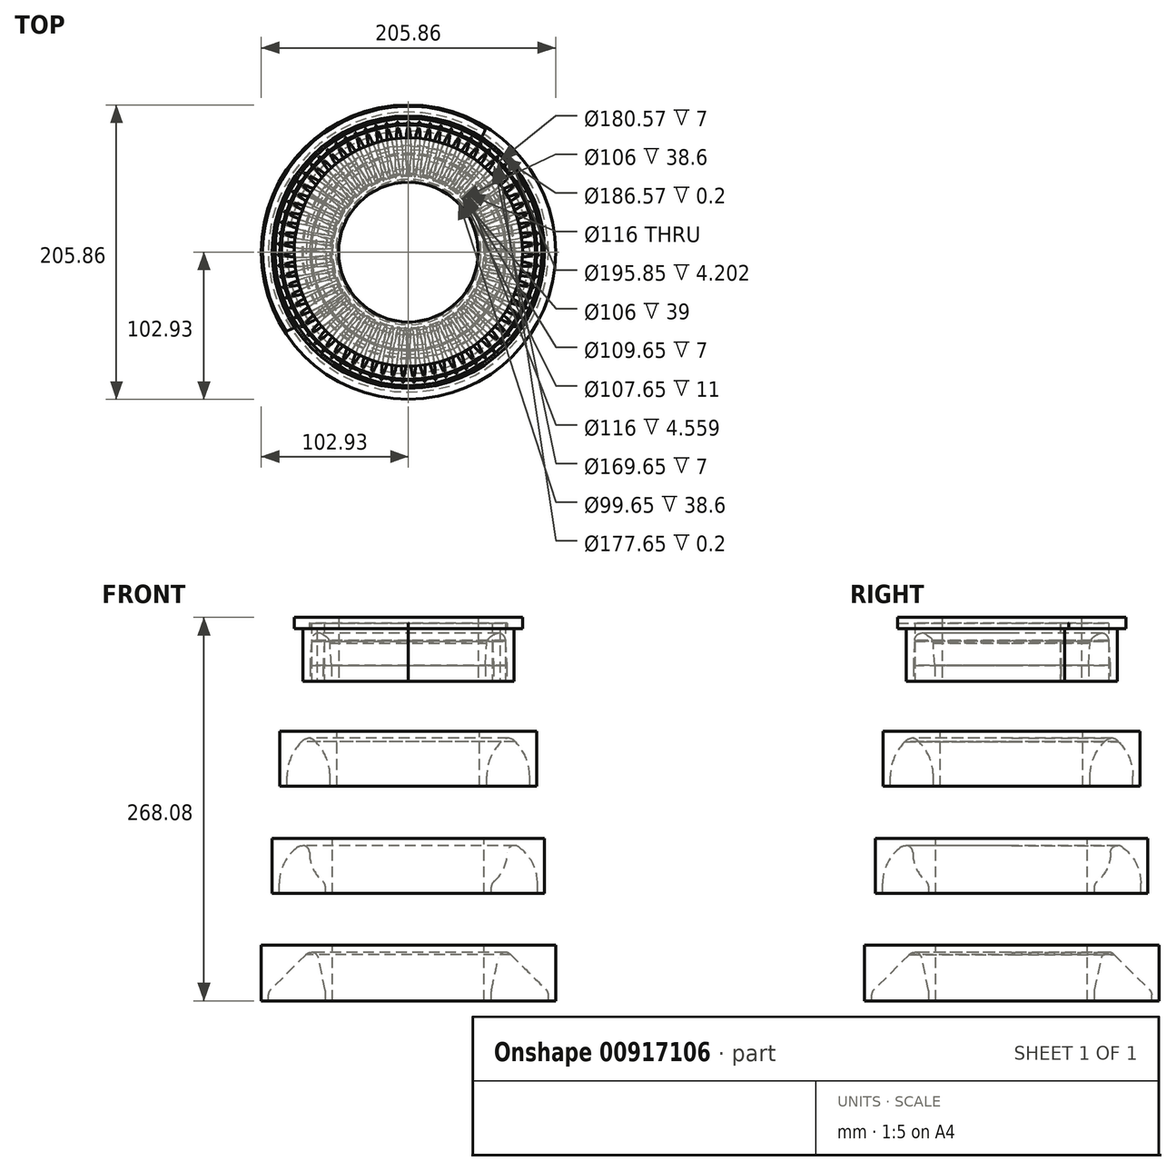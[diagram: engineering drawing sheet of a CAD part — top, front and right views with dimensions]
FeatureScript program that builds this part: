
annotation { "Feature Type Name" : "Feature", "Feature Type Description" : "" }
export const myFeature = defineFeature(function(context is Context, id is Id, definition is map)
    precondition{}
    {
        {
            var Q0;
            Q0=qCreatedBy(makeId("Front.planeOp"),FACE);
            var sketch = newSketch(context, id + "F0", { "sketchPlane" : qUnion([Q0])});
            skArc(sketch, "E0", {"start": v(57.08, 22.7) * mm, "mid": v(58.52, 23.67) * mm, "end": v(59.95, 24.66) * mm});
            skLineSegment(sketch, "E1", {"start": v(0, 0) * mm, "end": v(54.83, 0) * mm, "construction": true});
            skLineSegment(sketch, "E2", {"start": v(54.83, 0) * mm, "end": v(54.83, -7) * mm, "construction": true});
            skLineSegment(sketch, "E3", {"start": v(54.83, -7) * mm, "end": v(67.83, -7) * mm, "construction": true});
            skLineSegment(sketch, "E4", {"start": v(67.83, -7) * mm, "end": v(67.83, 0) * mm, "construction": true});
            skLineSegment(sketch, "E5", {"start": v(54.83, 0) * mm, "end": v(54.83, 3) * mm, "construction": true});
            skLineSegment(sketch, "E6", {"start": v(67.83, 0) * mm, "end": v(67.83, 3) * mm, "construction": true});
            skLineSegment(sketch, "E7", {"start": v(0, -3.7) * mm, "end": v(44, -3.7) * mm, "construction": true});
            skLineSegment(sketch, "E8", {"start": v(61.33, -7) * mm, "end": v(61.33, 37.52) * mm, "construction": true});
            skPoint(sketch, "E9.visualSharp", {"position": v(54.8, 21.25) * mm});
            skArc(sketch, "E9.filletArc", {"start": v(57.08, 22.7) * mm, "mid": v(55.43, 20.9) * mm, "end": v(54.83, 18.53) * mm});
            skPoint(sketch, "E10.visualSharp", {"position": v(67.8, 30.73) * mm});
            skArc(sketch, "E10.filletArc", {"start": v(67.83, 20.57) * mm, "mid": v(65.13, 25) * mm, "end": v(59.95, 24.66) * mm});
            skLineSegment(sketch, "E11.0", {"start": v(53.83, 0) * mm, "end": v(53.83, 3) * mm});
            skLineSegment(sketch, "E11.1", {"start": v(68.83, 0) * mm, "end": v(68.83, 3) * mm});
            skLineSegment(sketch, "E11.2", {"start": v(68.83, -8) * mm, "end": v(68.83, 0) * mm});
            skLineSegment(sketch, "E11.3", {"start": v(53.83, -8) * mm, "end": v(68.83, -8) * mm});
            skLineSegment(sketch, "E11.4", {"start": v(53.83, 0) * mm, "end": v(53.83, -8) * mm});
            skLineSegment(sketch, "E12", {"start": v(54.83, 18.53) * mm, "end": v(53.83, 3) * mm});
            skLineSegment(sketch, "E13", {"start": v(67.83, 20.57) * mm, "end": v(68.83, 3) * mm});
            skLineSegment(sketch, "E14", {"start": v(0, 0) * mm, "end": v(0, 24.2) * mm});
            skText(sketch, "E15", { "text": "Profile\n", "fontName": "OpenSans-Regular.ttf"});
            skLineSegment(sketch, "E16.0", {"start": v(48.83, 0) * mm, "end": v(48.83, -8) * mm});
            skLineSegment(sketch, "E16.1", {"start": v(48.83, 0) * mm, "end": v(48.83, 3.64) * mm});
            skLineSegment(sketch, "E16.5", {"start": v(73.83, -8) * mm, "end": v(73.83, 0) * mm});
            skLineSegment(sketch, "E17", {"start": v(48.83, 28.57) * mm, "end": v(73.83, 28.57) * mm});
            skLineSegment(sketch, "E18", {"start": v(73.83, 28.57) * mm, "end": v(73.83, 0) * mm});
            skLineSegment(sketch, "E19", {"start": v(48.83, 28.57) * mm, "end": v(48.83, 3.64) * mm});
            skLineSegment(sketch, "E20", {"start": v(53.83, -8) * mm, "end": v(48.83, -8) * mm});
            skLineSegment(sketch, "E21", {"start": v(68.83, -8) * mm, "end": v(73.83, -8) * mm});
            skLineSegment(sketch, "E22", {"start": v(0, -74.51) * mm, "end": v(54.82, -74.51) * mm, "construction": true});
            skLineSegment(sketch, "E23", {"start": v(54.83, -74.51) * mm, "end": v(54.83, -81.51) * mm});
            skLineSegment(sketch, "E24", {"start": v(54.83, -81.51) * mm, "end": v(84.83, -81.51) * mm});
            skLineSegment(sketch, "E25", {"start": v(54.83, -47.91) * mm, "end": v(121.36, -47.91) * mm, "construction": true});
            skArc(sketch, "E26", {"start": v(74.54, -50.2) * mm, "mid": v(69.83, -47.91) * mm, "end": v(65.11, -50.2) * mm});
            skLineSegment(sketch, "E27", {"start": v(69.83, -81.51) * mm, "end": v(69.83, -35.12) * mm, "construction": true});
            skLineSegment(sketch, "E28.MirrorCS", {"start": v(84.83, -74.51) * mm, "end": v(84.83, -81.51) * mm});
            skArc(sketch, "E29", {"start": v(84.83, -74.51) * mm, "mid": v(82.15, -61.31) * mm, "end": v(74.54, -50.2) * mm});
            skArc(sketch, "E30.MirrorCS", {"start": v(54.83, -74.51) * mm, "mid": v(57.5, -61.31) * mm, "end": v(65.11, -50.2) * mm});
            skLineSegment(sketch, "E31", {"start": v(0, -149.51) * mm, "end": v(58, -149.51) * mm, "construction": true});
            skLineSegment(sketch, "E32", {"start": v(58, -151.95) * mm, "end": v(58, -156.51) * mm});
            skLineSegment(sketch, "E33", {"start": v(58, -156.51) * mm, "end": v(90.28, -156.51) * mm});
            skLineSegment(sketch, "E34", {"start": v(58, -122.91) * mm, "end": v(116.03, -122.91) * mm, "construction": true});
            skArc(sketch, "E35", {"start": v(77.04, -123.84) * mm, "mid": v(71.85, -123.47) * mm, "end": v(69.14, -127.91) * mm});
            skLineSegment(sketch, "E36", {"start": v(74.14, -115.42) * mm, "end": v(74.14, -156.51) * mm, "construction": true});
            skLineSegment(sketch, "E37.MirrorCS", {"start": v(90.28, -149.51) * mm, "end": v(90.28, -156.51) * mm});
            skArc(sketch, "E38", {"start": v(90.28, -149.51) * mm, "mid": v(86.78, -135.07) * mm, "end": v(77.04, -123.84) * mm});
            skArc(sketch, "E39", {"start": v(59.77, -148.14) * mm, "mid": v(66.68, -139.06) * mm, "end": v(69.14, -127.91) * mm});
            skPoint(sketch, "E39.first.point", {"position": v(69.14, -127.91) * mm});
            skPoint(sketch, "E40.visualSharp", {"position": v(58, -149.51) * mm});
            skArc(sketch, "E40.filletArc", {"start": v(59.77, -148.14) * mm, "mid": v(58.46, -149.85) * mm, "end": v(58, -151.95) * mm});
            skLineSegment(sketch, "E41", {"start": v(0, -36.15) * mm, "end": v(0, -90.59) * mm});
            skLineSegment(sketch, "E42", {"start": v(0, -114.92) * mm, "end": v(0, -170.64) * mm});
            skLineSegment(sketch, "E43", {"start": v(84.83, -81.51) * mm, "end": v(89.83, -81.51) * mm});
            skLineSegment(sketch, "E44", {"start": v(89.83, -81.51) * mm, "end": v(89.83, -42.91) * mm});
            skLineSegment(sketch, "E45", {"start": v(89.83, -42.91) * mm, "end": v(49.83, -42.91) * mm});
            skLineSegment(sketch, "E46.MirrorCS", {"start": v(49.83, -81.51) * mm, "end": v(49.83, -42.91) * mm});
            skLineSegment(sketch, "E47", {"start": v(49.83, -81.51) * mm, "end": v(54.83, -81.51) * mm});
            skLineSegment(sketch, "E48", {"start": v(53, -117.91) * mm, "end": v(95.28, -117.91) * mm});
            skLineSegment(sketch, "E49", {"start": v(90.28, -156.51) * mm, "end": v(95.28, -156.51) * mm});
            skLineSegment(sketch, "E50", {"start": v(95.28, -156.51) * mm, "end": v(95.28, -117.91) * mm});
            skLineSegment(sketch, "E51.MirrorCS", {"start": v(53, -156.51) * mm, "end": v(53, -117.91) * mm});
            skLineSegment(sketch, "E52", {"start": v(53, -156.51) * mm, "end": v(58, -156.51) * mm});
            skText(sketch, "E53", { "text": "A", "fontName": "OpenSans-Regular.ttf"});
            skText(sketch, "E54", { "text": "B", "fontName": "OpenSans-Regular.ttf"});
            skText(sketch, "E55", { "text": "C", "fontName": "OpenSans-Regular.ttf"});
            skLineSegment(sketch, "E56", {"start": v(0, -224.51) * mm, "end": v(58, -224.51) * mm, "construction": true});
            skLineSegment(sketch, "E57", {"start": v(58, -225.04) * mm, "end": v(58, -231.51) * mm});
            skLineSegment(sketch, "E58", {"start": v(58, -231.51) * mm, "end": v(94.93, -231.51) * mm});
            skLineSegment(sketch, "E59", {"start": v(61.33, -231.51) * mm, "end": v(61.33, -197.91) * mm, "construction": true});
            skLineSegment(sketch, "E60", {"start": v(61.33, -197.91) * mm, "end": v(109.36, -245.95) * mm, "construction": true});
            skLineSegment(sketch, "E61", {"start": v(61.33, -197.91) * mm, "end": v(64.33, -197.91) * mm, "construction": true});
            skLineSegment(sketch, "E62", {"start": v(94.93, -231.51) * mm, "end": v(97.93, -231.51) * mm});
            skLineSegment(sketch, "E63", {"start": v(62.95, -201.46) * mm, "end": v(58.11, -224) * mm});
            skArc(sketch, "E64.filletArc", {"start": v(71.53, -199.14) * mm, "mid": v(66.53, -197.69) * mm, "end": v(62.95, -201.46) * mm});
            skPoint(sketch, "E65.visualSharp", {"position": v(58, -224.51) * mm});
            skArc(sketch, "E65.filletArc", {"start": v(58.11, -224) * mm, "mid": v(58.03, -224.52) * mm, "end": v(58, -225.04) * mm});
            skLineSegment(sketch, "E66", {"start": v(97.93, -231.51) * mm, "end": v(97.93, -227.31) * mm});
            skLineSegment(sketch, "E67", {"start": v(71.53, -199.14) * mm, "end": v(96.44, -223.75) * mm});
            skPoint(sketch, "E68.visualSharp", {"position": v(97.93, -225.22) * mm});
            skArc(sketch, "E68.filletArc", {"start": v(97.93, -227.31) * mm, "mid": v(97.54, -225.38) * mm, "end": v(96.44, -223.75) * mm});
            skText(sketch, "E69", { "text": "D", "fontName": "OpenSans-Regular.ttf"});
            skLineSegment(sketch, "E70", {"start": v(58, -231.51) * mm, "end": v(53, -231.51) * mm});
            skLineSegment(sketch, "E71", {"start": v(53, -231.51) * mm, "end": v(53, -192.51) * mm});
            skLineSegment(sketch, "E72", {"start": v(97.93, -231.51) * mm, "end": v(102.93, -231.51) * mm});
            skLineSegment(sketch, "E73", {"start": v(102.93, -231.51) * mm, "end": v(102.93, -192.51) * mm});
            skLineSegment(sketch, "E74", {"start": v(102.93, -192.51) * mm, "end": v(53, -192.51) * mm});
            const initialGuessF0  = {"E15": [0.04907, 0.0562, 1, 0, 0.00809], "E53": [0.10484, -0.00592, 1, 0, 0.01864], "E54": [0.11039, -0.0753, 1, 0, 0.023], "E55": [0.10761, -0.15302, 1, 0, 0.02657], "E69": [0.11061, -0.22251, 1, 0, 0.02251]};
            skSetInitialGuess(sketch, initialGuessF0);
            skSolve(sketch);
        }
        {
            var Q0;
            Q0=makeQuery(id+"F0.imprint","IMPRINT",FACE,{"disambiguationData":[TD([[makeQuery(id+"F0.imprint","IMPRINT",EDGE,{"derivedFrom":sQuery(id+"F0.wireOp",EDGE,"E0")}),-1.0]])]});
            var Q1;
            Q1=sQuery(id+"F0.wireOp",EDGE,"E14");
            revolve(context, id + "F1", {"surfaceOperationType" : NewSurfaceOperationType.NEW, "entities" : qUnion([Q0]), "axis" : qUnion([Q1]), "revolveType" : RevolveType.FULL});
        }
        {
            var Q0;
            Q0=makeQuery(id+"F0.imprint","IMPRINT",FACE,{"disambiguationData":[TD([[makeQuery(id+"F0.imprint","IMPRINT",EDGE,{"derivedFrom":sQuery(id+"F0.wireOp",EDGE,"E0")}),1.0]])]});
            var Q1;
            Q1=sQuery(id+"F0.wireOp",EDGE,"E14");
            revolve(context, id + "F2", {"surfaceOperationType" : NewSurfaceOperationType.NEW, "entities" : qUnion([Q0]), "axis" : qUnion([Q1]), "revolveType" : RevolveType.FULL});
        }
        {
            var Q0;
            Q0=makeQuery(id+"F2.opRevolve","SWEPT_FACE",FACE,{"disambiguationData":[OSD([sQuery(id+"F0.wireOp",EDGE,"E17")])]});
            var sketch = newSketch(context, id + "F3", { "sketchPlane" : qUnion([Q0])});
            skLineSegment(sketch, "E75", {"start": v(0, 0) * mm, "end": v(0, 102.73) * mm, "construction": true});
            skLineSegment(sketch, "E76", {"start": v(0, 0) * mm, "end": v(97.94, -56.55) * mm, "construction": true});
            skLineSegment(sketch, "E77", {"start": v(0, 0) * mm, "end": v(-77.07, -44.5) * mm, "construction": true});
            skCircle(sketch, "E78.0", {"center": v(0, 0) * mm, "radius": 48.83 * mm});
            skCircle(sketch, "E79.0", {"center": v(0, 0) * mm, "radius": 73.83 * mm, "construction": true});
            skCircle(sketch, "E80", {"center": v(0, 0) * mm, "radius": 79.83 * mm});
            skSolve(sketch);
        }
        {
            var Q0;
            Q0=makeQuery(id+"F3.imprint","IMPRINT",FACE,{"disambiguationData":[TD([[makeQuery(id+"F3.imprint","IMPRINT",EDGE,{"derivedFrom":sQuery(id+"F3.wireOp",EDGE,"E80")}),1.0]])]});
            var Q1;
            Q1=makeQuery(id+"F3.imprint","IMPRINT",FACE,{"disambiguationData":[TD([[makeQuery(id+"F3.imprint","IMPRINT",EDGE,{"derivedFrom":sQuery(id+"F3.wireOp",EDGE,"E78.0")}),1.0]])]});
            extrude(context, id + "F4", {"entities" : qUnion([Q0, Q1]), "operationType" : NewBodyOperationType.ADD, "depth" : 8 * mm, "offsetDistance" : 25 * mm});
        }
        {
            var Q0;
            Q0=makeQuery(id+"F2.opRevolve","SWEPT_FACE",FACE,{"disambiguationData":[OSD([sQuery(id+"F0.wireOp",EDGE,"E20")])]});
            var sketch = newSketch(context, id + "F5", { "sketchPlane" : qUnion([Q0])});
            skLineSegment(sketch, "E81", {"start": v(0, 0) * mm, "end": v(0, 60.65) * mm, "construction": true});
            skLineSegment(sketch, "E82", {"start": v(0, 0) * mm, "end": v(-52.01, -30.03) * mm, "construction": true});
            skLineSegment(sketch, "E83", {"start": v(0, 0) * mm, "end": v(51.36, -29.65) * mm, "construction": true});
            skCircle(sketch, "E84.0", {"center": v(0, 0) * mm, "radius": 67.83 * mm});
            skCircle(sketch, "E85.0", {"center": v(0, 0) * mm, "radius": 79.83 * mm});
            skLineSegment(sketch, "E86", {"start": v(-58.8, -33.9) * mm, "end": v(-69.16, -39.87) * mm});
            skLineSegment(sketch, "E87", {"start": v(58.76, -33.98) * mm, "end": v(69.1, -39.96) * mm});
            skLineSegment(sketch, "E88", {"start": v(0, 67.88) * mm, "end": v(0, 79.83) * mm});
            skArc(sketch, "E89.0", {"start": v(-58.8, -33.9) * mm, "mid": v(-0.07, -67.87) * mm, "end": v(58.73, -34.02) * mm});
            skLineSegment(sketch, "E90.0", {"start": v(-58.83, -33.85) * mm, "end": v(-69.18, -39.83) * mm});
            skLineSegment(sketch, "E91.0", {"start": v(58.73, -34.02) * mm, "end": v(69.08, -40) * mm});
            skArc(sketch, "E92.trimOffspring", {"start": v(58.76, -33.98) * mm, "mid": v(58.8, 33.9) * mm, "end": v(0.05, 67.87) * mm});
            skLineSegment(sketch, "E93.0", {"start": v(0.05, 67.87) * mm, "end": v(0.05, 79.82) * mm});
            skPoint(sketch, "E94.orphan", {"position": v(0, 67.83) * mm});
            skArc(sketch, "E95.trimOffspring", {"start": v(0, 67.88) * mm, "mid": v(-58.76, 33.98) * mm, "end": v(-58.83, -33.85) * mm});
            skSolve(sketch);
        }
        {
            var Q0;
            Q0=makeQuery(id+"F5.imprint","IMPRINT",FACE,{"disambiguationData":[TD([[makeQuery(id+"F5.imprint","IMPRINT",EDGE,{"derivedFrom":sQuery(id+"F5.wireOp",EDGE,"E84.0")}),-1.0]])]});
            extrude(context, id + "F6", {"entities" : qUnion([Q0]), "operationType" : NewBodyOperationType.REMOVE, "oppositeDirection" : true, "depth" : 59 * mm, "offsetDistance" : 25 * mm});
        }
        {
            var Q0;
            Q0=qCreatedBy(makeId("Front.planeOp"),FACE);
            var sketch = newSketch(context, id + "F7", { "sketchPlane" : qUnion([Q0])});
            skLineSegment(sketch, "E96.0", {"start": v(-79.83, 28.57) * mm, "end": v(0, 28.57) * mm, "construction": true});
            skLineSegment(sketch, "E96.1", {"start": v(-79.83, 36.57) * mm, "end": v(0, 36.57) * mm, "construction": true});
            skLineSegment(sketch, "E96.2", {"start": v(0.05, 28.57) * mm, "end": v(79.83, 28.57) * mm, "construction": true});
            skLineSegment(sketch, "E96.3", {"start": v(0.05, 36.57) * mm, "end": v(79.83, 36.57) * mm, "construction": true});
            skLineSegment(sketch, "E97", {"start": v(-79.83, 28.57) * mm, "end": v(-79.83, 36.57) * mm, "construction": true});
            skLineSegment(sketch, "E98", {"start": v(79.83, 28.57) * mm, "end": v(79.83, 36.57) * mm, "construction": true});
            skLineSegment(sketch, "E99", {"start": v(79.83, 32.57) * mm, "end": v(-79.83, 32.57) * mm});
            skLineSegment(sketch, "E100.0", {"start": v(79.83, 32.62) * mm, "end": v(-79.83, 32.62) * mm});
            skLineSegment(sketch, "E101", {"start": v(-79.83, 32.57) * mm, "end": v(-79.83, 32.62) * mm});
            skLineSegment(sketch, "E102", {"start": v(79.83, 32.57) * mm, "end": v(79.83, 32.62) * mm});
            skSolve(sketch);
        }
        {
            var Q0;
            Q0 = qSketchRegion(id + "F7", true);
            extrude(context, id + "F8", {"entities" : qUnion([Q0]), "operationType" : NewBodyOperationType.REMOVE, "endBound" : BoundingType.SYMMETRIC, "depth" : 166 * mm, "offsetDistance" : 25 * mm});
        }
        {
            var Q0;
            Q0=makeQuery(id+"F3.imprint","IMPRINT",FACE,{"disambiguationData":[TD([[makeQuery(id+"F3.imprint","IMPRINT",EDGE,{"derivedFrom":sQuery(id+"F3.wireOp",EDGE,"E78.0")}),1.0]])]});
            var Q1;
            Q1=makeQuery(id+"F3.imprint","IMPRINT",FACE,{"disambiguationData":[TD([[makeQuery(id+"F3.imprint","IMPRINT",EDGE,{"derivedFrom":sQuery(id+"F3.wireOp",EDGE,"E80")}),1.0]])]});
            extrude(context, id + "F9", {"entities" : qUnion([Q0, Q1]), "operationType" : NewBodyOperationType.ADD, "depth" : 8 * mm, "offsetDistance" : 25 * mm, "hasSecondDirection" : true, "secondDirectionOppositeDirection" : false, "secondDirectionDepth" : 4 * mm});
        }
        {
            var Q0;
            Q0=qCreatedBy(makeId("Front.planeOp"),FACE);
            var sketch = newSketch(context, id + "F10", { "sketchPlane" : qUnion([Q0])});
            skLineSegment(sketch, "E103.bottom", {"start": v(-92.97, 59.22) * mm, "end": v(50.29, 59.22) * mm});
            skLineSegment(sketch, "E103.top", {"start": v(-92.97, -47.6) * mm, "end": v(50.29, -47.6) * mm});
            skLineSegment(sketch, "E103.left", {"start": v(-92.97, 59.22) * mm, "end": v(-92.97, -47.6) * mm});
            skLineSegment(sketch, "E103.right", {"start": v(50.29, 59.22) * mm, "end": v(50.29, -47.6) * mm});
            skSolve(sketch);
        }
        {
            var Q0;
            Q0=makeQuery(id+"F0.imprint","IMPRINT",FACE,{"disambiguationData":[TD([[makeQuery(id+"F0.imprint","IMPRINT",EDGE,{"derivedFrom":sQuery(id+"F0.wireOp",EDGE,"E23")}),1.0]])]});
            var Q1;
            Q1=sQuery(id+"F0.wireOp",EDGE,"E41");
            revolve(context, id + "F11", {"surfaceOperationType" : NewSurfaceOperationType.NEW, "entities" : qUnion([Q0]), "axis" : qUnion([Q1]), "revolveType" : RevolveType.FULL});
        }
        {
            var Q0;
            Q0=makeQuery(id+"F0.imprint","IMPRINT",FACE,{"disambiguationData":[TD([[makeQuery(id+"F0.imprint","IMPRINT",EDGE,{"derivedFrom":sQuery(id+"F0.wireOp",EDGE,"E32")}),1.0]])]});
            var Q1;
            Q1=sQuery(id+"F0.wireOp",EDGE,"E42");
            revolve(context, id + "F12", {"surfaceOperationType" : NewSurfaceOperationType.NEW, "entities" : qUnion([Q0]), "axis" : qUnion([Q1]), "revolveType" : RevolveType.FULL});
        }
        {
            var Q0;
            Q0=makeQuery(id+"F0.imprint","IMPRINT",FACE,{"disambiguationData":[TD([[makeQuery(id+"F0.imprint","IMPRINT",EDGE,{"derivedFrom":sQuery(id+"F0.wireOp",EDGE,"E23")}),-1.0]])]});
            var Q1;
            Q1=makeQuery(id+"F0.imprint","IMPRINT",FACE,{"disambiguationData":[TD([[makeQuery(id+"F0.imprint","IMPRINT",EDGE,{"derivedFrom":sQuery(id+"F0.wireOp",EDGE,"E32")}),-1.0]])]});
            var Q2;
            Q2=sQuery(id+"F0.wireOp",EDGE,"E41");
            revolve(context, id + "F13", {"surfaceOperationType" : NewSurfaceOperationType.NEW, "entities" : qUnion([Q0, Q1]), "axis" : qUnion([Q2]), "revolveType" : RevolveType.FULL});
        }
        {
            var Q0;
            Q0=makeQuery(id+"F13.opRevolve","SWEPT_FACE",FACE,{"disambiguationData":[OSD([sQuery(id+"F0.wireOp",EDGE,"E45")])]});
            var sketch = newSketch(context, id + "F14", { "sketchPlane" : qUnion([Q0])});
            skCircle(sketch, "E104.0", {"center": v(0, 0) * mm, "radius": 49.83 * mm});
            skCircle(sketch, "E104.1", {"center": v(0, 0) * mm, "radius": 89.83 * mm});
            skCircle(sketch, "E105.0", {"center": v(0, 0) * mm, "radius": 88.83 * mm});
            skCircle(sketch, "E106.0", {"center": v(0, 0) * mm, "radius": 50.83 * mm});
            skLineSegment(sketch, "E107", {"start": v(0, 50.83) * mm, "end": v(0, 88.83) * mm, "construction": true});
            skLineSegment(sketch, "E108", {"start": v(2, 97.11) * mm, "end": v(2, 40.33) * mm, "construction": true});
            skCircle(sketch, "E109.0", {"center": v(0, 0) * mm, "radius": 86.83 * mm, "construction": true});
            skCircle(sketch, "E110.0", {"center": v(0, 0) * mm, "radius": 52.83 * mm, "construction": true});
            skEllipse(sketch, "E111", {"center": v(0, 69.83) * mm, "majorRadius": 17 * mm, "minorRadius": 2 * mm, "majorAxis": v(0, -1)});
            skEllipse(sketch, "E112.1.0", {"center": v(-5.84, 69.58) * mm, "majorRadius": 17 * mm, "minorRadius": 2 * mm, "majorAxis": v(0.08, -1)});
            skEllipse(sketch, "E112.2.0", {"center": v(-11.64, 68.85) * mm, "majorRadius": 17 * mm, "minorRadius": 2 * mm, "majorAxis": v(0.17, -0.99)});
            skEllipse(sketch, "E113.1.3.0", {"center": v(-17.36, 67.63) * mm, "majorRadius": 17 * mm, "minorRadius": 2 * mm, "majorAxis": v(0.25, -0.97)});
            skEllipse(sketch, "E113.1.4.0", {"center": v(-22.96, 65.94) * mm, "majorRadius": 17 * mm, "minorRadius": 2 * mm, "majorAxis": v(0.33, -0.94)});
            skEllipse(sketch, "E113.1.5.0", {"center": v(-28.4, 63.79) * mm, "majorRadius": 17 * mm, "minorRadius": 2 * mm, "majorAxis": v(0.4, -0.91)});
            skEllipse(sketch, "E113.1.6.0", {"center": v(-33.64, 61.19) * mm, "majorRadius": 17 * mm, "minorRadius": 2 * mm, "majorAxis": v(0.48, -0.88)});
            skEllipse(sketch, "E113.1.7.0", {"center": v(-38.64, 58.16) * mm, "majorRadius": 17 * mm, "minorRadius": 2 * mm, "majorAxis": v(0.55, -0.83)});
            skEllipse(sketch, "E113.1.8.0", {"center": v(-43.37, 54.72) * mm, "majorRadius": 17 * mm, "minorRadius": 2 * mm, "majorAxis": v(0.62, -0.78)});
            skEllipse(sketch, "E113.1.9.0", {"center": v(-47.8, 50.9) * mm, "majorRadius": 17 * mm, "minorRadius": 2 * mm, "majorAxis": v(0.68, -0.73)});
            skEllipse(sketch, "E113.1.10.0", {"center": v(-51.9, 46.72) * mm, "majorRadius": 17 * mm, "minorRadius": 2 * mm, "majorAxis": v(0.74, -0.67)});
            skEllipse(sketch, "E113.1.11.0", {"center": v(-55.62, 42.22) * mm, "majorRadius": 17 * mm, "minorRadius": 2 * mm, "majorAxis": v(0.8, -0.6)});
            skEllipse(sketch, "E113.1.12.0", {"center": v(-58.96, 37.41) * mm, "majorRadius": 17 * mm, "minorRadius": 2 * mm, "majorAxis": v(0.84, -0.54)});
            skEllipse(sketch, "E113.1.13.0", {"center": v(-61.88, 32.35) * mm, "majorRadius": 17 * mm, "minorRadius": 2 * mm, "majorAxis": v(0.89, -0.46)});
            skEllipse(sketch, "E113.1.14.0", {"center": v(-64.37, 27.06) * mm, "majorRadius": 17 * mm, "minorRadius": 2 * mm, "majorAxis": v(0.92, -0.39)});
            skEllipse(sketch, "E113.1.15.0", {"center": v(-66.4, 21.58) * mm, "majorRadius": 17 * mm, "minorRadius": 2 * mm, "majorAxis": v(0.95, -0.3)});
            skEllipse(sketch, "E113.1.16.0", {"center": v(-67.98, 15.94) * mm, "majorRadius": 17 * mm, "minorRadius": 2 * mm, "majorAxis": v(0.97, -0.23)});
            skEllipse(sketch, "E113.1.17.0", {"center": v(-69.08, 10.2) * mm, "majorRadius": 17 * mm, "minorRadius": 2 * mm, "majorAxis": v(0.99, -0.15)});
            skEllipse(sketch, "E113.1.18.0", {"center": v(-69.69, 4.38) * mm, "majorRadius": 17 * mm, "minorRadius": 2 * mm, "majorAxis": v(1, -0.06)});
            skEllipse(sketch, "E113.1.19.0", {"center": v(-69.8, -1.46) * mm, "majorRadius": 17 * mm, "minorRadius": 2 * mm, "majorAxis": v(1, 0.02)});
            skEllipse(sketch, "E113.1.20.0", {"center": v(-69.44, -7.3) * mm, "majorRadius": 17 * mm, "minorRadius": 2 * mm, "majorAxis": v(1, 0.1)});
            skEllipse(sketch, "E113.1.21.0", {"center": v(-68.59, -13.08) * mm, "majorRadius": 17 * mm, "minorRadius": 2 * mm, "majorAxis": v(0.98, 0.19)});
            skEllipse(sketch, "E113.1.22.0", {"center": v(-67.25, -18.78) * mm, "majorRadius": 17 * mm, "minorRadius": 2 * mm, "majorAxis": v(0.96, 0.27)});
            skEllipse(sketch, "E113.1.23.0", {"center": v(-65.45, -24.34) * mm, "majorRadius": 17 * mm, "minorRadius": 2 * mm, "majorAxis": v(0.94, 0.35)});
            skEllipse(sketch, "E113.1.24.0", {"center": v(-63.18, -29.73) * mm, "majorRadius": 17 * mm, "minorRadius": 2 * mm, "majorAxis": v(0.9, 0.43)});
            skEllipse(sketch, "E113.1.25.0", {"center": v(-60.47, -34.91) * mm, "majorRadius": 17 * mm, "minorRadius": 2 * mm, "majorAxis": v(0.87, 0.5)});
            skEllipse(sketch, "E113.1.26.0", {"center": v(-57.34, -39.85) * mm, "majorRadius": 17 * mm, "minorRadius": 2 * mm, "majorAxis": v(0.82, 0.57)});
            skEllipse(sketch, "E113.1.27.0", {"center": v(-53.8, -44.5) * mm, "majorRadius": 17 * mm, "minorRadius": 2 * mm, "majorAxis": v(0.77, 0.64)});
            skEllipse(sketch, "E113.1.28.0", {"center": v(-49.89, -48.85) * mm, "majorRadius": 17 * mm, "minorRadius": 2 * mm, "majorAxis": v(0.71, 0.7)});
            skEllipse(sketch, "E113.1.29.0", {"center": v(-45.63, -52.86) * mm, "majorRadius": 17 * mm, "minorRadius": 2 * mm, "majorAxis": v(0.65, 0.76)});
            skEllipse(sketch, "E113.1.30.0", {"center": v(-41.04, -56.49) * mm, "majorRadius": 17 * mm, "minorRadius": 2 * mm, "majorAxis": v(0.59, 0.8)});
            skEllipse(sketch, "E113.1.31.0", {"center": v(-36.17, -59.73) * mm, "majorRadius": 17 * mm, "minorRadius": 2 * mm, "majorAxis": v(0.52, 0.86)});
            skEllipse(sketch, "E113.1.32.0", {"center": v(-31.05, -62.54) * mm, "majorRadius": 17 * mm, "minorRadius": 2 * mm, "majorAxis": v(0.44, 0.9)});
            skEllipse(sketch, "E113.1.33.0", {"center": v(-25.7, -64.92) * mm, "majorRadius": 17 * mm, "minorRadius": 2 * mm, "majorAxis": v(0.37, 0.93)});
            skEllipse(sketch, "E113.1.34.0", {"center": v(-20.18, -66.84) * mm, "majorRadius": 17 * mm, "minorRadius": 2 * mm, "majorAxis": v(0.29, 0.96)});
            skEllipse(sketch, "E113.1.35.0", {"center": v(-14.52, -68.3) * mm, "majorRadius": 17 * mm, "minorRadius": 2 * mm, "majorAxis": v(0.2, 0.98)});
            skEllipse(sketch, "E113.1.36.0", {"center": v(-8.75, -69.27) * mm, "majorRadius": 17 * mm, "minorRadius": 2 * mm, "majorAxis": v(0.13, 1)});
            skEllipse(sketch, "E113.1.37.0", {"center": v(-2.92, -69.76) * mm, "majorRadius": 17 * mm, "minorRadius": 2 * mm, "majorAxis": v(0.04, 1)});
            skEllipse(sketch, "E113.1.38.0", {"center": v(2.92, -69.76) * mm, "majorRadius": 17 * mm, "minorRadius": 2 * mm, "majorAxis": v(-0.04, 1)});
            skEllipse(sketch, "E113.1.39.0", {"center": v(8.75, -69.27) * mm, "majorRadius": 17 * mm, "minorRadius": 2 * mm, "majorAxis": v(-0.13, 1)});
            skEllipse(sketch, "E113.1.40.0", {"center": v(14.52, -68.3) * mm, "majorRadius": 17 * mm, "minorRadius": 2 * mm, "majorAxis": v(-0.2, 0.98)});
            skEllipse(sketch, "E113.1.41.0", {"center": v(20.18, -66.84) * mm, "majorRadius": 17 * mm, "minorRadius": 2 * mm, "majorAxis": v(-0.29, 0.96)});
            skEllipse(sketch, "E113.1.42.0", {"center": v(25.7, -64.92) * mm, "majorRadius": 17 * mm, "minorRadius": 2 * mm, "majorAxis": v(-0.37, 0.93)});
            skEllipse(sketch, "E113.1.43.0", {"center": v(31.05, -62.54) * mm, "majorRadius": 17 * mm, "minorRadius": 2 * mm, "majorAxis": v(-0.44, 0.9)});
            skEllipse(sketch, "E113.1.44.0", {"center": v(36.17, -59.73) * mm, "majorRadius": 17 * mm, "minorRadius": 2 * mm, "majorAxis": v(-0.52, 0.86)});
            skEllipse(sketch, "E113.1.45.0", {"center": v(41.04, -56.49) * mm, "majorRadius": 17 * mm, "minorRadius": 2 * mm, "majorAxis": v(-0.59, 0.8)});
            skEllipse(sketch, "E113.1.46.0", {"center": v(45.63, -52.86) * mm, "majorRadius": 17 * mm, "minorRadius": 2 * mm, "majorAxis": v(-0.65, 0.76)});
            skEllipse(sketch, "E113.1.47.0", {"center": v(49.89, -48.85) * mm, "majorRadius": 17 * mm, "minorRadius": 2 * mm, "majorAxis": v(-0.71, 0.7)});
            skEllipse(sketch, "E113.1.48.0", {"center": v(53.8, -44.5) * mm, "majorRadius": 17 * mm, "minorRadius": 2 * mm, "majorAxis": v(-0.77, 0.64)});
            skEllipse(sketch, "E113.1.49.0", {"center": v(57.34, -39.85) * mm, "majorRadius": 17 * mm, "minorRadius": 2 * mm, "majorAxis": v(-0.82, 0.57)});
            skEllipse(sketch, "E113.1.50.0", {"center": v(60.47, -34.91) * mm, "majorRadius": 17 * mm, "minorRadius": 2 * mm, "majorAxis": v(-0.87, 0.5)});
            skEllipse(sketch, "E113.1.51.0", {"center": v(63.18, -29.73) * mm, "majorRadius": 17 * mm, "minorRadius": 2 * mm, "majorAxis": v(-0.9, 0.43)});
            skEllipse(sketch, "E113.1.52.0", {"center": v(65.45, -24.34) * mm, "majorRadius": 17 * mm, "minorRadius": 2 * mm, "majorAxis": v(-0.94, 0.35)});
            skEllipse(sketch, "E113.1.53.0", {"center": v(67.25, -18.78) * mm, "majorRadius": 17 * mm, "minorRadius": 2 * mm, "majorAxis": v(-0.96, 0.27)});
            skEllipse(sketch, "E113.1.54.0", {"center": v(68.59, -13.08) * mm, "majorRadius": 17 * mm, "minorRadius": 2 * mm, "majorAxis": v(-0.98, 0.19)});
            skEllipse(sketch, "E113.1.55.0", {"center": v(69.44, -7.3) * mm, "majorRadius": 17 * mm, "minorRadius": 2 * mm, "majorAxis": v(-1, 0.1)});
            skEllipse(sketch, "E113.1.56.0", {"center": v(69.8, -1.46) * mm, "majorRadius": 17 * mm, "minorRadius": 2 * mm, "majorAxis": v(-1, 0.02)});
            skEllipse(sketch, "E113.1.57.0", {"center": v(69.69, 4.38) * mm, "majorRadius": 17 * mm, "minorRadius": 2 * mm, "majorAxis": v(-1, -0.06)});
            skEllipse(sketch, "E113.1.58.0", {"center": v(69.08, 10.2) * mm, "majorRadius": 17 * mm, "minorRadius": 2 * mm, "majorAxis": v(-0.99, -0.15)});
            skEllipse(sketch, "E113.1.59.0", {"center": v(67.98, 15.94) * mm, "majorRadius": 17 * mm, "minorRadius": 2 * mm, "majorAxis": v(-0.97, -0.23)});
            skEllipse(sketch, "E113.1.60.0", {"center": v(66.4, 21.58) * mm, "majorRadius": 17 * mm, "minorRadius": 2 * mm, "majorAxis": v(-0.95, -0.3)});
            skEllipse(sketch, "E113.1.61.0", {"center": v(64.37, 27.06) * mm, "majorRadius": 17 * mm, "minorRadius": 2 * mm, "majorAxis": v(-0.92, -0.39)});
            skEllipse(sketch, "E113.1.62.0", {"center": v(61.88, 32.35) * mm, "majorRadius": 17 * mm, "minorRadius": 2 * mm, "majorAxis": v(-0.89, -0.46)});
            skEllipse(sketch, "E113.1.63.0", {"center": v(58.96, 37.41) * mm, "majorRadius": 17 * mm, "minorRadius": 2 * mm, "majorAxis": v(-0.84, -0.54)});
            skEllipse(sketch, "E113.1.64.0", {"center": v(55.62, 42.22) * mm, "majorRadius": 17 * mm, "minorRadius": 2 * mm, "majorAxis": v(-0.8, -0.6)});
            skEllipse(sketch, "E113.1.65.0", {"center": v(51.9, 46.72) * mm, "majorRadius": 17 * mm, "minorRadius": 2 * mm, "majorAxis": v(-0.74, -0.67)});
            skEllipse(sketch, "E113.1.66.0", {"center": v(47.8, 50.9) * mm, "majorRadius": 17 * mm, "minorRadius": 2 * mm, "majorAxis": v(-0.68, -0.73)});
            skEllipse(sketch, "E113.1.67.0", {"center": v(43.37, 54.72) * mm, "majorRadius": 17 * mm, "minorRadius": 2 * mm, "majorAxis": v(-0.62, -0.78)});
            skEllipse(sketch, "E113.1.68.0", {"center": v(38.64, 58.16) * mm, "majorRadius": 17 * mm, "minorRadius": 2 * mm, "majorAxis": v(-0.55, -0.83)});
            skEllipse(sketch, "E113.1.69.0", {"center": v(33.64, 61.19) * mm, "majorRadius": 17 * mm, "minorRadius": 2 * mm, "majorAxis": v(-0.48, -0.88)});
            skEllipse(sketch, "E113.1.70.0", {"center": v(28.4, 63.79) * mm, "majorRadius": 17 * mm, "minorRadius": 2 * mm, "majorAxis": v(-0.4, -0.91)});
            skEllipse(sketch, "E113.1.71.0", {"center": v(22.96, 65.94) * mm, "majorRadius": 17 * mm, "minorRadius": 2 * mm, "majorAxis": v(-0.33, -0.94)});
            skEllipse(sketch, "E113.1.72.0", {"center": v(17.36, 67.63) * mm, "majorRadius": 17 * mm, "minorRadius": 2 * mm, "majorAxis": v(-0.25, -0.97)});
            skEllipse(sketch, "E113.1.73.0", {"center": v(11.64, 68.85) * mm, "majorRadius": 17 * mm, "minorRadius": 2 * mm, "majorAxis": v(-0.17, -0.99)});
            skEllipse(sketch, "E113.1.74.0", {"center": v(5.84, 69.58) * mm, "majorRadius": 17 * mm, "minorRadius": 2 * mm, "majorAxis": v(-0.08, -1)});
            skSolve(sketch);
        }
        {
            var Q0;
            Q0=makeQuery(id+"F14.imprint","IMPRINT",FACE,{"disambiguationData":[TD([[makeQuery(id+"F14.imprint","IMPRINT",EDGE,{"derivedFrom":sQuery(id+"F14.wireOp",EDGE,"E105.0")}),1.0]])]});
            extrude(context, id + "F15", {"entities" : qUnion([Q0]), "operationType" : NewBodyOperationType.REMOVE, "oppositeDirection" : true, "depth" : .2 * mm, "offsetDistance" : 25 * mm});
        }
        {
            var Q0;
            Q0=makeQuery(id+"F13.opRevolve","SWEPT_FACE",FACE,{"disambiguationData":[OSD([sQuery(id+"F0.wireOp",EDGE,"E48")])]});
            var sketch = newSketch(context, id + "F16", { "sketchPlane" : qUnion([Q0])});
            skCircle(sketch, "E114.0", {"center": v(0, 0) * mm, "radius": 53 * mm});
            skCircle(sketch, "E114.1", {"center": v(0, 0) * mm, "radius": 95.28 * mm});
            skLineSegment(sketch, "E115", {"start": v(0, 53) * mm, "end": v(0, 95.28) * mm, "construction": true});
            skCircle(sketch, "E116.0", {"center": v(0, 0) * mm, "radius": 55 * mm});
            skCircle(sketch, "E117.0", {"center": v(0, 0) * mm, "radius": 93.28 * mm});
            skCircle(sketch, "E118.0", {"center": v(0, 0) * mm, "radius": 57 * mm, "construction": true});
            skCircle(sketch, "E119.0", {"center": v(0, 0) * mm, "radius": 91.28 * mm, "construction": true});
            skLineSegment(sketch, "E120", {"start": v(2, 98.13) * mm, "end": v(2, 38.24) * mm, "construction": true});
            skEllipse(sketch, "E121", {"center": v(0, 74.14) * mm, "majorRadius": 17.14 * mm, "minorRadius": 2 * mm, "majorAxis": v(0, -1)});
            skEllipse(sketch, "E122.1.0", {"center": v(-6.2, 73.88) * mm, "majorRadius": 17.14 * mm, "minorRadius": 2 * mm, "majorAxis": v(0.08, -1)});
            skEllipse(sketch, "E122.2.0", {"center": v(-12.36, 73.1) * mm, "majorRadius": 17.14 * mm, "minorRadius": 2 * mm, "majorAxis": v(0.17, -0.99)});
            skEllipse(sketch, "E123.1.3.0", {"center": v(-18.44, 71.81) * mm, "majorRadius": 17.14 * mm, "minorRadius": 2 * mm, "majorAxis": v(0.25, -0.97)});
            skEllipse(sketch, "E123.1.4.0", {"center": v(-24.38, 70.02) * mm, "majorRadius": 17.14 * mm, "minorRadius": 2 * mm, "majorAxis": v(0.33, -0.94)});
            skEllipse(sketch, "E123.1.5.0", {"center": v(-30.16, 67.73) * mm, "majorRadius": 17.14 * mm, "minorRadius": 2 * mm, "majorAxis": v(0.4, -0.91)});
            skEllipse(sketch, "E123.1.6.0", {"center": v(-35.72, 64.97) * mm, "majorRadius": 17.14 * mm, "minorRadius": 2 * mm, "majorAxis": v(0.48, -0.88)});
            skEllipse(sketch, "E123.1.7.0", {"center": v(-41.03, 61.75) * mm, "majorRadius": 17.14 * mm, "minorRadius": 2 * mm, "majorAxis": v(0.55, -0.83)});
            skEllipse(sketch, "E123.1.8.0", {"center": v(-46.05, 58.1) * mm, "majorRadius": 17.14 * mm, "minorRadius": 2 * mm, "majorAxis": v(0.62, -0.78)});
            skEllipse(sketch, "E123.1.9.0", {"center": v(-50.75, 54.05) * mm, "majorRadius": 17.14 * mm, "minorRadius": 2 * mm, "majorAxis": v(0.68, -0.73)});
            skEllipse(sketch, "E123.1.10.0", {"center": v(-55.1, 49.61) * mm, "majorRadius": 17.14 * mm, "minorRadius": 2 * mm, "majorAxis": v(0.74, -0.67)});
            skEllipse(sketch, "E123.1.11.0", {"center": v(-59.06, 44.83) * mm, "majorRadius": 17.14 * mm, "minorRadius": 2 * mm, "majorAxis": v(0.8, -0.6)});
            skEllipse(sketch, "E123.1.12.0", {"center": v(-62.6, 39.73) * mm, "majorRadius": 17.14 * mm, "minorRadius": 2 * mm, "majorAxis": v(0.84, -0.54)});
            skEllipse(sketch, "E123.1.13.0", {"center": v(-65.7, 34.35) * mm, "majorRadius": 17.14 * mm, "minorRadius": 2 * mm, "majorAxis": v(0.89, -0.46)});
            skEllipse(sketch, "E123.1.14.0", {"center": v(-68.35, 28.73) * mm, "majorRadius": 17.14 * mm, "minorRadius": 2 * mm, "majorAxis": v(0.92, -0.39)});
            skEllipse(sketch, "E123.1.15.0", {"center": v(-70.51, 22.91) * mm, "majorRadius": 17.14 * mm, "minorRadius": 2 * mm, "majorAxis": v(0.95, -0.3)});
            skEllipse(sketch, "E123.1.16.0", {"center": v(-72.18, 16.93) * mm, "majorRadius": 17.14 * mm, "minorRadius": 2 * mm, "majorAxis": v(0.97, -0.23)});
            skEllipse(sketch, "E123.1.17.0", {"center": v(-73.35, 10.83) * mm, "majorRadius": 17.14 * mm, "minorRadius": 2 * mm, "majorAxis": v(0.99, -0.15)});
            skEllipse(sketch, "E123.1.18.0", {"center": v(-74, 4.66) * mm, "majorRadius": 17.14 * mm, "minorRadius": 2 * mm, "majorAxis": v(1, -0.06)});
            skEllipse(sketch, "E123.1.19.0", {"center": v(-74.13, -1.55) * mm, "majorRadius": 17.14 * mm, "minorRadius": 2 * mm, "majorAxis": v(1, 0.02)});
            skEllipse(sketch, "E123.1.20.0", {"center": v(-73.74, -7.75) * mm, "majorRadius": 17.14 * mm, "minorRadius": 2 * mm, "majorAxis": v(1, 0.1)});
            skEllipse(sketch, "E123.1.21.0", {"center": v(-72.83, -13.9) * mm, "majorRadius": 17.14 * mm, "minorRadius": 2 * mm, "majorAxis": v(0.98, 0.19)});
            skEllipse(sketch, "E123.1.22.0", {"center": v(-71.41, -19.94) * mm, "majorRadius": 17.14 * mm, "minorRadius": 2 * mm, "majorAxis": v(0.96, 0.27)});
            skEllipse(sketch, "E123.1.23.0", {"center": v(-69.5, -25.84) * mm, "majorRadius": 17.14 * mm, "minorRadius": 2 * mm, "majorAxis": v(0.94, 0.35)});
            skEllipse(sketch, "E123.1.24.0", {"center": v(-67.09, -31.57) * mm, "majorRadius": 17.14 * mm, "minorRadius": 2 * mm, "majorAxis": v(0.9, 0.43)});
            skEllipse(sketch, "E123.1.25.0", {"center": v(-64.2, -37.07) * mm, "majorRadius": 17.14 * mm, "minorRadius": 2 * mm, "majorAxis": v(0.87, 0.5)});
            skEllipse(sketch, "E123.1.26.0", {"center": v(-60.88, -42.31) * mm, "majorRadius": 17.14 * mm, "minorRadius": 2 * mm, "majorAxis": v(0.82, 0.57)});
            skEllipse(sketch, "E123.1.27.0", {"center": v(-57.13, -47.26) * mm, "majorRadius": 17.14 * mm, "minorRadius": 2 * mm, "majorAxis": v(0.77, 0.64)});
            skEllipse(sketch, "E123.1.28.0", {"center": v(-52.97, -51.87) * mm, "majorRadius": 17.14 * mm, "minorRadius": 2 * mm, "majorAxis": v(0.71, 0.7)});
            skEllipse(sketch, "E123.1.29.0", {"center": v(-48.45, -56.13) * mm, "majorRadius": 17.14 * mm, "minorRadius": 2 * mm, "majorAxis": v(0.65, 0.76)});
            skEllipse(sketch, "E123.1.30.0", {"center": v(-43.58, -59.98) * mm, "majorRadius": 17.14 * mm, "minorRadius": 2 * mm, "majorAxis": v(0.59, 0.8)});
            skEllipse(sketch, "E123.1.31.0", {"center": v(-38.4, -63.42) * mm, "majorRadius": 17.14 * mm, "minorRadius": 2 * mm, "majorAxis": v(0.52, 0.86)});
            skEllipse(sketch, "E123.1.32.0", {"center": v(-32.97, -66.4) * mm, "majorRadius": 17.14 * mm, "minorRadius": 2 * mm, "majorAxis": v(0.44, 0.9)});
            skEllipse(sketch, "E123.1.33.0", {"center": v(-27.3, -68.94) * mm, "majorRadius": 17.14 * mm, "minorRadius": 2 * mm, "majorAxis": v(0.37, 0.93)});
            skEllipse(sketch, "E123.1.34.0", {"center": v(-21.43, -70.98) * mm, "majorRadius": 17.14 * mm, "minorRadius": 2 * mm, "majorAxis": v(0.29, 0.96)});
            skEllipse(sketch, "E123.1.35.0", {"center": v(-15.41, -72.52) * mm, "majorRadius": 17.14 * mm, "minorRadius": 2 * mm, "majorAxis": v(0.2, 0.98)});
            skEllipse(sketch, "E123.1.36.0", {"center": v(-9.3, -73.56) * mm, "majorRadius": 17.14 * mm, "minorRadius": 2 * mm, "majorAxis": v(0.13, 1)});
            skEllipse(sketch, "E123.1.37.0", {"center": v(-3.1, -74.08) * mm, "majorRadius": 17.14 * mm, "minorRadius": 2 * mm, "majorAxis": v(0.04, 1)});
            skEllipse(sketch, "E123.1.38.0", {"center": v(3.1, -74.08) * mm, "majorRadius": 17.14 * mm, "minorRadius": 2 * mm, "majorAxis": v(-0.04, 1)});
            skEllipse(sketch, "E123.1.39.0", {"center": v(9.3, -73.56) * mm, "majorRadius": 17.14 * mm, "minorRadius": 2 * mm, "majorAxis": v(-0.13, 1)});
            skEllipse(sketch, "E123.1.40.0", {"center": v(15.41, -72.52) * mm, "majorRadius": 17.14 * mm, "minorRadius": 2 * mm, "majorAxis": v(-0.2, 0.98)});
            skEllipse(sketch, "E123.1.41.0", {"center": v(21.43, -70.98) * mm, "majorRadius": 17.14 * mm, "minorRadius": 2 * mm, "majorAxis": v(-0.29, 0.96)});
            skEllipse(sketch, "E123.1.42.0", {"center": v(27.3, -68.94) * mm, "majorRadius": 17.14 * mm, "minorRadius": 2 * mm, "majorAxis": v(-0.37, 0.93)});
            skEllipse(sketch, "E123.1.43.0", {"center": v(32.97, -66.4) * mm, "majorRadius": 17.14 * mm, "minorRadius": 2 * mm, "majorAxis": v(-0.44, 0.9)});
            skEllipse(sketch, "E123.1.44.0", {"center": v(38.4, -63.42) * mm, "majorRadius": 17.14 * mm, "minorRadius": 2 * mm, "majorAxis": v(-0.52, 0.86)});
            skEllipse(sketch, "E123.1.45.0", {"center": v(43.58, -59.98) * mm, "majorRadius": 17.14 * mm, "minorRadius": 2 * mm, "majorAxis": v(-0.59, 0.8)});
            skEllipse(sketch, "E123.1.46.0", {"center": v(48.45, -56.13) * mm, "majorRadius": 17.14 * mm, "minorRadius": 2 * mm, "majorAxis": v(-0.65, 0.76)});
            skEllipse(sketch, "E123.1.47.0", {"center": v(52.97, -51.87) * mm, "majorRadius": 17.14 * mm, "minorRadius": 2 * mm, "majorAxis": v(-0.71, 0.7)});
            skEllipse(sketch, "E123.1.48.0", {"center": v(57.13, -47.26) * mm, "majorRadius": 17.14 * mm, "minorRadius": 2 * mm, "majorAxis": v(-0.77, 0.64)});
            skEllipse(sketch, "E123.1.49.0", {"center": v(60.88, -42.31) * mm, "majorRadius": 17.14 * mm, "minorRadius": 2 * mm, "majorAxis": v(-0.82, 0.57)});
            skEllipse(sketch, "E123.1.50.0", {"center": v(64.2, -37.07) * mm, "majorRadius": 17.14 * mm, "minorRadius": 2 * mm, "majorAxis": v(-0.87, 0.5)});
            skEllipse(sketch, "E123.1.51.0", {"center": v(67.09, -31.57) * mm, "majorRadius": 17.14 * mm, "minorRadius": 2 * mm, "majorAxis": v(-0.9, 0.43)});
            skEllipse(sketch, "E123.1.52.0", {"center": v(69.5, -25.84) * mm, "majorRadius": 17.14 * mm, "minorRadius": 2 * mm, "majorAxis": v(-0.94, 0.35)});
            skEllipse(sketch, "E123.1.53.0", {"center": v(71.41, -19.94) * mm, "majorRadius": 17.14 * mm, "minorRadius": 2 * mm, "majorAxis": v(-0.96, 0.27)});
            skEllipse(sketch, "E123.1.54.0", {"center": v(72.83, -13.9) * mm, "majorRadius": 17.14 * mm, "minorRadius": 2 * mm, "majorAxis": v(-0.98, 0.19)});
            skEllipse(sketch, "E123.1.55.0", {"center": v(73.74, -7.75) * mm, "majorRadius": 17.14 * mm, "minorRadius": 2 * mm, "majorAxis": v(-1, 0.1)});
            skEllipse(sketch, "E123.1.56.0", {"center": v(74.13, -1.55) * mm, "majorRadius": 17.14 * mm, "minorRadius": 2 * mm, "majorAxis": v(-1, 0.02)});
            skEllipse(sketch, "E123.1.57.0", {"center": v(74, 4.66) * mm, "majorRadius": 17.14 * mm, "minorRadius": 2 * mm, "majorAxis": v(-1, -0.06)});
            skEllipse(sketch, "E123.1.58.0", {"center": v(73.35, 10.83) * mm, "majorRadius": 17.14 * mm, "minorRadius": 2 * mm, "majorAxis": v(-0.99, -0.15)});
            skEllipse(sketch, "E123.1.59.0", {"center": v(72.18, 16.93) * mm, "majorRadius": 17.14 * mm, "minorRadius": 2 * mm, "majorAxis": v(-0.97, -0.23)});
            skEllipse(sketch, "E123.1.60.0", {"center": v(70.51, 22.91) * mm, "majorRadius": 17.14 * mm, "minorRadius": 2 * mm, "majorAxis": v(-0.95, -0.3)});
            skEllipse(sketch, "E123.1.61.0", {"center": v(68.35, 28.73) * mm, "majorRadius": 17.14 * mm, "minorRadius": 2 * mm, "majorAxis": v(-0.92, -0.39)});
            skEllipse(sketch, "E123.1.62.0", {"center": v(65.7, 34.35) * mm, "majorRadius": 17.14 * mm, "minorRadius": 2 * mm, "majorAxis": v(-0.89, -0.46)});
            skEllipse(sketch, "E123.1.63.0", {"center": v(62.6, 39.73) * mm, "majorRadius": 17.14 * mm, "minorRadius": 2 * mm, "majorAxis": v(-0.84, -0.54)});
            skEllipse(sketch, "E123.1.64.0", {"center": v(59.06, 44.83) * mm, "majorRadius": 17.14 * mm, "minorRadius": 2 * mm, "majorAxis": v(-0.8, -0.6)});
            skEllipse(sketch, "E123.1.65.0", {"center": v(55.1, 49.61) * mm, "majorRadius": 17.14 * mm, "minorRadius": 2 * mm, "majorAxis": v(-0.74, -0.67)});
            skEllipse(sketch, "E123.1.66.0", {"center": v(50.75, 54.05) * mm, "majorRadius": 17.14 * mm, "minorRadius": 2 * mm, "majorAxis": v(-0.68, -0.73)});
            skEllipse(sketch, "E123.1.67.0", {"center": v(46.05, 58.1) * mm, "majorRadius": 17.14 * mm, "minorRadius": 2 * mm, "majorAxis": v(-0.62, -0.78)});
            skEllipse(sketch, "E123.1.68.0", {"center": v(41.03, 61.75) * mm, "majorRadius": 17.14 * mm, "minorRadius": 2 * mm, "majorAxis": v(-0.55, -0.83)});
            skEllipse(sketch, "E123.1.69.0", {"center": v(35.72, 64.97) * mm, "majorRadius": 17.14 * mm, "minorRadius": 2 * mm, "majorAxis": v(-0.48, -0.88)});
            skEllipse(sketch, "E123.1.70.0", {"center": v(30.16, 67.73) * mm, "majorRadius": 17.14 * mm, "minorRadius": 2 * mm, "majorAxis": v(-0.4, -0.91)});
            skEllipse(sketch, "E123.1.71.0", {"center": v(24.38, 70.02) * mm, "majorRadius": 17.14 * mm, "minorRadius": 2 * mm, "majorAxis": v(-0.33, -0.94)});
            skEllipse(sketch, "E123.1.72.0", {"center": v(18.44, 71.81) * mm, "majorRadius": 17.14 * mm, "minorRadius": 2 * mm, "majorAxis": v(-0.25, -0.97)});
            skEllipse(sketch, "E123.1.73.0", {"center": v(12.36, 73.1) * mm, "majorRadius": 17.14 * mm, "minorRadius": 2 * mm, "majorAxis": v(-0.17, -0.99)});
            skEllipse(sketch, "E123.1.74.0", {"center": v(6.2, 73.88) * mm, "majorRadius": 17.14 * mm, "minorRadius": 2 * mm, "majorAxis": v(-0.08, -1)});
            skSolve(sketch);
        }
        {
            var Q0;
            Q0=makeQuery(id+"F16.imprint","IMPRINT",FACE,{"disambiguationData":[TD([[makeQuery(id+"F16.imprint","IMPRINT",EDGE,{"derivedFrom":sQuery(id+"F16.wireOp",EDGE,"E116.0")}),-1.0]])]});
            extrude(context, id + "F17", {"entities" : qUnion([Q0]), "operationType" : NewBodyOperationType.REMOVE, "oppositeDirection" : true, "depth" : .2 * mm, "offsetDistance" : 25 * mm});
        }
        {
            var Q0;
            Q0=makeQuery(id+"F0.imprint","IMPRINT",FACE,{"disambiguationData":[TD([[makeQuery(id+"F0.imprint","IMPRINT",EDGE,{"derivedFrom":sQuery(id+"F0.wireOp",EDGE,"E57")}),1.0]])]});
            var Q1;
            Q1=sQuery(id+"F0.wireOp",EDGE,"E42");
            revolve(context, id + "F18", {"surfaceOperationType" : NewSurfaceOperationType.NEW, "entities" : qUnion([Q0]), "axis" : qUnion([Q1]), "revolveType" : RevolveType.FULL});
        }
        {
            var Q0;
            Q0=makeQuery(id+"F0.imprint","IMPRINT",FACE,{"disambiguationData":[TD([[makeQuery(id+"F0.imprint","IMPRINT",EDGE,{"derivedFrom":sQuery(id+"F0.wireOp",EDGE,"E57")}),-1.0]])]});
            var Q1;
            Q1=sQuery(id+"F0.wireOp",EDGE,"E42");
            revolve(context, id + "F19", {"surfaceOperationType" : NewSurfaceOperationType.NEW, "entities" : qUnion([Q0]), "axis" : qUnion([Q1]), "revolveType" : RevolveType.FULL});
        }
        {
            var Q0;
            Q0=makeQuery(id+"F19.opRevolve","SWEPT_FACE",FACE,{"disambiguationData":[OSD([sQuery(id+"F0.wireOp",EDGE,"E74")])]});
            var sketch = newSketch(context, id + "F20", { "sketchPlane" : qUnion([Q0])});
            skCircle(sketch, "E124.0", {"center": v(0, 0) * mm, "radius": 102.93 * mm});
            skCircle(sketch, "E124.1", {"center": v(0, 0) * mm, "radius": 53 * mm});
            skCircle(sketch, "E125.0", {"center": v(0, 0) * mm, "radius": 54 * mm});
            skCircle(sketch, "E126.0", {"center": v(0, 0) * mm, "radius": 55 * mm, "construction": true});
            skCircle(sketch, "E127.0", {"center": v(0, 0) * mm, "radius": 101.93 * mm});
            skCircle(sketch, "E128.0", {"center": v(0, 0) * mm, "radius": 100.93 * mm, "construction": true});
            skLineSegment(sketch, "E129", {"start": v(0, 55) * mm, "end": v(0, 100.93) * mm, "construction": true});
            skLineSegment(sketch, "E130", {"start": v(2, 109.82) * mm, "end": v(2, 47.04) * mm, "construction": true});
            skEllipse(sketch, "E131", {"center": v(0, 77.96) * mm, "majorRadius": 24.55 * mm, "minorRadius": 2 * mm, "majorAxis": v(0, -1)});
            skEllipse(sketch, "E132.1.0", {"center": v(-6.18, 77.66) * mm, "majorRadius": 24.55 * mm, "minorRadius": 2 * mm, "majorAxis": v(0.08, -1)});
            skEllipse(sketch, "E132.2.0", {"center": v(-12.31, 76.87) * mm, "majorRadius": 24.55 * mm, "minorRadius": 2 * mm, "majorAxis": v(0.16, -0.99)});
            skPoint(sketch, "E132.center", {"position": v(0.8, -0.8) * mm});
            skEllipse(sketch, "E133.1.3.0", {"center": v(-18.36, 75.6) * mm, "majorRadius": 24.55 * mm, "minorRadius": 2 * mm, "majorAxis": v(0.23, -0.97)});
            skEllipse(sketch, "E133.1.4.0", {"center": v(-24.3, 73.86) * mm, "majorRadius": 24.55 * mm, "minorRadius": 2 * mm, "majorAxis": v(0.3, -0.95)});
            skEllipse(sketch, "E133.1.5.0", {"center": v(-30.08, 71.66) * mm, "majorRadius": 24.55 * mm, "minorRadius": 2 * mm, "majorAxis": v(0.38, -0.92)});
            skEllipse(sketch, "E133.1.6.0", {"center": v(-35.67, 69.02) * mm, "majorRadius": 24.55 * mm, "minorRadius": 2 * mm, "majorAxis": v(0.45, -0.9)});
            skEllipse(sketch, "E133.1.7.0", {"center": v(-41.03, 65.94) * mm, "majorRadius": 24.55 * mm, "minorRadius": 2 * mm, "majorAxis": v(0.52, -0.85)});
            skEllipse(sketch, "E133.1.8.0", {"center": v(-46.14, 62.45) * mm, "majorRadius": 24.55 * mm, "minorRadius": 2 * mm, "majorAxis": v(0.59, -0.8)});
            skEllipse(sketch, "E133.1.9.0", {"center": v(-50.96, 58.58) * mm, "majorRadius": 24.55 * mm, "minorRadius": 2 * mm, "majorAxis": v(0.65, -0.76)});
            skEllipse(sketch, "E133.1.10.0", {"center": v(-55.46, 54.33) * mm, "majorRadius": 24.55 * mm, "minorRadius": 2 * mm, "majorAxis": v(0.7, -0.7)});
            skEllipse(sketch, "E133.1.11.0", {"center": v(-59.6, 49.75) * mm, "majorRadius": 24.55 * mm, "minorRadius": 2 * mm, "majorAxis": v(0.76, -0.65)});
            skEllipse(sketch, "E133.1.12.0", {"center": v(-63.39, 44.86) * mm, "majorRadius": 24.55 * mm, "minorRadius": 2 * mm, "majorAxis": v(0.8, -0.59)});
            skEllipse(sketch, "E133.1.13.0", {"center": v(-66.77, 39.68) * mm, "majorRadius": 24.55 * mm, "minorRadius": 2 * mm, "majorAxis": v(0.85, -0.52)});
            skEllipse(sketch, "E133.1.14.0", {"center": v(-69.74, 34.25) * mm, "majorRadius": 24.55 * mm, "minorRadius": 2 * mm, "majorAxis": v(0.9, -0.45)});
            skEllipse(sketch, "E133.1.15.0", {"center": v(-72.27, 28.61) * mm, "majorRadius": 24.55 * mm, "minorRadius": 2 * mm, "majorAxis": v(0.92, -0.38)});
            skEllipse(sketch, "E133.1.16.0", {"center": v(-74.35, 22.79) * mm, "majorRadius": 24.55 * mm, "minorRadius": 2 * mm, "majorAxis": v(0.95, -0.3)});
            skEllipse(sketch, "E133.1.17.0", {"center": v(-75.97, 16.82) * mm, "majorRadius": 24.55 * mm, "minorRadius": 2 * mm, "majorAxis": v(0.97, -0.23)});
            skEllipse(sketch, "E133.1.18.0", {"center": v(-77.12, 10.74) * mm, "majorRadius": 24.55 * mm, "minorRadius": 2 * mm, "majorAxis": v(0.99, -0.16)});
            skEllipse(sketch, "E133.1.19.0", {"center": v(-77.78, 4.6) * mm, "majorRadius": 24.55 * mm, "minorRadius": 2 * mm, "majorAxis": v(1, -0.08)});
            skEllipse(sketch, "E133.1.20.0", {"center": v(-77.96, -1.59) * mm, "majorRadius": 24.55 * mm, "minorRadius": 2 * mm, "majorAxis": v(1, 0)});
            skEllipse(sketch, "E133.1.21.0", {"center": v(-77.66, -7.76) * mm, "majorRadius": 24.55 * mm, "minorRadius": 2 * mm, "majorAxis": v(1, 0.08)});
            skEllipse(sketch, "E133.1.22.0", {"center": v(-76.87, -13.9) * mm, "majorRadius": 24.55 * mm, "minorRadius": 2 * mm, "majorAxis": v(0.99, 0.16)});
            skEllipse(sketch, "E133.1.23.0", {"center": v(-75.6, -19.95) * mm, "majorRadius": 24.55 * mm, "minorRadius": 2 * mm, "majorAxis": v(0.97, 0.23)});
            skEllipse(sketch, "E133.1.24.0", {"center": v(-73.86, -25.89) * mm, "majorRadius": 24.55 * mm, "minorRadius": 2 * mm, "majorAxis": v(0.95, 0.3)});
            skEllipse(sketch, "E133.1.25.0", {"center": v(-71.66, -31.67) * mm, "majorRadius": 24.55 * mm, "minorRadius": 2 * mm, "majorAxis": v(0.92, 0.38)});
            skEllipse(sketch, "E133.1.26.0", {"center": v(-69.02, -37.26) * mm, "majorRadius": 24.55 * mm, "minorRadius": 2 * mm, "majorAxis": v(0.9, 0.45)});
            skEllipse(sketch, "E133.1.27.0", {"center": v(-65.94, -42.62) * mm, "majorRadius": 24.55 * mm, "minorRadius": 2 * mm, "majorAxis": v(0.85, 0.52)});
            skEllipse(sketch, "E133.1.28.0", {"center": v(-62.45, -47.73) * mm, "majorRadius": 24.55 * mm, "minorRadius": 2 * mm, "majorAxis": v(0.8, 0.59)});
            skEllipse(sketch, "E133.1.29.0", {"center": v(-58.58, -52.55) * mm, "majorRadius": 24.55 * mm, "minorRadius": 2 * mm, "majorAxis": v(0.76, 0.65)});
            skEllipse(sketch, "E133.1.30.0", {"center": v(-54.33, -57.04) * mm, "majorRadius": 24.55 * mm, "minorRadius": 2 * mm, "majorAxis": v(0.7, 0.7)});
            skEllipse(sketch, "E133.1.31.0", {"center": v(-49.75, -61.2) * mm, "majorRadius": 24.55 * mm, "minorRadius": 2 * mm, "majorAxis": v(0.65, 0.76)});
            skEllipse(sketch, "E133.1.32.0", {"center": v(-44.86, -64.98) * mm, "majorRadius": 24.55 * mm, "minorRadius": 2 * mm, "majorAxis": v(0.59, 0.8)});
            skEllipse(sketch, "E133.1.33.0", {"center": v(-39.68, -68.36) * mm, "majorRadius": 24.55 * mm, "minorRadius": 2 * mm, "majorAxis": v(0.52, 0.85)});
            skEllipse(sketch, "E133.1.34.0", {"center": v(-34.25, -71.33) * mm, "majorRadius": 24.55 * mm, "minorRadius": 2 * mm, "majorAxis": v(0.45, 0.9)});
            skEllipse(sketch, "E133.1.35.0", {"center": v(-28.61, -73.86) * mm, "majorRadius": 24.55 * mm, "minorRadius": 2 * mm, "majorAxis": v(0.38, 0.92)});
            skEllipse(sketch, "E133.1.36.0", {"center": v(-22.79, -75.94) * mm, "majorRadius": 24.55 * mm, "minorRadius": 2 * mm, "majorAxis": v(0.3, 0.95)});
            skEllipse(sketch, "E133.1.37.0", {"center": v(-16.82, -77.56) * mm, "majorRadius": 24.55 * mm, "minorRadius": 2 * mm, "majorAxis": v(0.23, 0.97)});
            skEllipse(sketch, "E133.1.38.0", {"center": v(-10.74, -78.7) * mm, "majorRadius": 24.55 * mm, "minorRadius": 2 * mm, "majorAxis": v(0.16, 0.99)});
            skEllipse(sketch, "E133.1.39.0", {"center": v(-4.6, -79.37) * mm, "majorRadius": 24.55 * mm, "minorRadius": 2 * mm, "majorAxis": v(0.08, 1)});
            skEllipse(sketch, "E133.1.40.0", {"center": v(1.59, -79.55) * mm, "majorRadius": 24.55 * mm, "minorRadius": 2 * mm, "majorAxis": v(0, 1)});
            skEllipse(sketch, "E133.1.41.0", {"center": v(7.76, -79.24) * mm, "majorRadius": 24.55 * mm, "minorRadius": 2 * mm, "majorAxis": v(-0.08, 1)});
            skEllipse(sketch, "E133.1.42.0", {"center": v(13.9, -78.46) * mm, "majorRadius": 24.55 * mm, "minorRadius": 2 * mm, "majorAxis": v(-0.16, 0.99)});
            skEllipse(sketch, "E133.1.43.0", {"center": v(19.95, -77.19) * mm, "majorRadius": 24.55 * mm, "minorRadius": 2 * mm, "majorAxis": v(-0.23, 0.97)});
            skEllipse(sketch, "E133.1.44.0", {"center": v(25.89, -75.45) * mm, "majorRadius": 24.55 * mm, "minorRadius": 2 * mm, "majorAxis": v(-0.3, 0.95)});
            skEllipse(sketch, "E133.1.45.0", {"center": v(31.67, -73.25) * mm, "majorRadius": 24.55 * mm, "minorRadius": 2 * mm, "majorAxis": v(-0.38, 0.92)});
            skEllipse(sketch, "E133.1.46.0", {"center": v(37.26, -70.6) * mm, "majorRadius": 24.55 * mm, "minorRadius": 2 * mm, "majorAxis": v(-0.45, 0.9)});
            skEllipse(sketch, "E133.1.47.0", {"center": v(42.62, -67.53) * mm, "majorRadius": 24.55 * mm, "minorRadius": 2 * mm, "majorAxis": v(-0.52, 0.85)});
            skEllipse(sketch, "E133.1.48.0", {"center": v(47.73, -64.04) * mm, "majorRadius": 24.55 * mm, "minorRadius": 2 * mm, "majorAxis": v(-0.59, 0.8)});
            skEllipse(sketch, "E133.1.49.0", {"center": v(52.55, -60.16) * mm, "majorRadius": 24.55 * mm, "minorRadius": 2 * mm, "majorAxis": v(-0.65, 0.76)});
            skEllipse(sketch, "E133.1.50.0", {"center": v(57.04, -55.92) * mm, "majorRadius": 24.55 * mm, "minorRadius": 2 * mm, "majorAxis": v(-0.7, 0.7)});
            skEllipse(sketch, "E133.1.51.0", {"center": v(61.2, -51.34) * mm, "majorRadius": 24.55 * mm, "minorRadius": 2 * mm, "majorAxis": v(-0.76, 0.65)});
            skEllipse(sketch, "E133.1.52.0", {"center": v(64.98, -46.44) * mm, "majorRadius": 24.55 * mm, "minorRadius": 2 * mm, "majorAxis": v(-0.8, 0.59)});
            skEllipse(sketch, "E133.1.53.0", {"center": v(68.36, -41.27) * mm, "majorRadius": 24.55 * mm, "minorRadius": 2 * mm, "majorAxis": v(-0.85, 0.52)});
            skEllipse(sketch, "E133.1.54.0", {"center": v(71.33, -35.84) * mm, "majorRadius": 24.55 * mm, "minorRadius": 2 * mm, "majorAxis": v(-0.9, 0.45)});
            skEllipse(sketch, "E133.1.55.0", {"center": v(73.86, -30.2) * mm, "majorRadius": 24.55 * mm, "minorRadius": 2 * mm, "majorAxis": v(-0.92, 0.38)});
            skEllipse(sketch, "E133.1.56.0", {"center": v(75.94, -24.38) * mm, "majorRadius": 24.55 * mm, "minorRadius": 2 * mm, "majorAxis": v(-0.95, 0.3)});
            skEllipse(sketch, "E133.1.57.0", {"center": v(77.56, -18.4) * mm, "majorRadius": 24.55 * mm, "minorRadius": 2 * mm, "majorAxis": v(-0.97, 0.23)});
            skEllipse(sketch, "E133.1.58.0", {"center": v(78.7, -12.33) * mm, "majorRadius": 24.55 * mm, "minorRadius": 2 * mm, "majorAxis": v(-0.99, 0.16)});
            skEllipse(sketch, "E133.1.59.0", {"center": v(79.37, -6.18) * mm, "majorRadius": 24.55 * mm, "minorRadius": 2 * mm, "majorAxis": v(-1, 0.08)});
            skEllipse(sketch, "E133.1.60.0", {"center": v(79.55, 0) * mm, "majorRadius": 24.55 * mm, "minorRadius": 2 * mm, "majorAxis": v(-1, 0)});
            skEllipse(sketch, "E133.1.61.0", {"center": v(79.24, 6.18) * mm, "majorRadius": 24.55 * mm, "minorRadius": 2 * mm, "majorAxis": v(-1, -0.08)});
            skEllipse(sketch, "E133.1.62.0", {"center": v(78.46, 12.31) * mm, "majorRadius": 24.55 * mm, "minorRadius": 2 * mm, "majorAxis": v(-0.99, -0.16)});
            skEllipse(sketch, "E133.1.63.0", {"center": v(77.19, 18.36) * mm, "majorRadius": 24.55 * mm, "minorRadius": 2 * mm, "majorAxis": v(-0.97, -0.23)});
            skEllipse(sketch, "E133.1.64.0", {"center": v(75.45, 24.3) * mm, "majorRadius": 24.55 * mm, "minorRadius": 2 * mm, "majorAxis": v(-0.95, -0.3)});
            skEllipse(sketch, "E133.1.65.0", {"center": v(73.25, 30.08) * mm, "majorRadius": 24.55 * mm, "minorRadius": 2 * mm, "majorAxis": v(-0.92, -0.38)});
            skEllipse(sketch, "E133.1.66.0", {"center": v(70.6, 35.67) * mm, "majorRadius": 24.55 * mm, "minorRadius": 2 * mm, "majorAxis": v(-0.9, -0.45)});
            skEllipse(sketch, "E133.1.67.0", {"center": v(67.53, 41.03) * mm, "majorRadius": 24.55 * mm, "minorRadius": 2 * mm, "majorAxis": v(-0.85, -0.52)});
            skEllipse(sketch, "E133.1.68.0", {"center": v(64.04, 46.14) * mm, "majorRadius": 24.55 * mm, "minorRadius": 2 * mm, "majorAxis": v(-0.8, -0.59)});
            skEllipse(sketch, "E133.1.69.0", {"center": v(60.16, 50.96) * mm, "majorRadius": 24.55 * mm, "minorRadius": 2 * mm, "majorAxis": v(-0.76, -0.65)});
            skEllipse(sketch, "E133.1.70.0", {"center": v(55.92, 55.46) * mm, "majorRadius": 24.55 * mm, "minorRadius": 2 * mm, "majorAxis": v(-0.7, -0.7)});
            skEllipse(sketch, "E133.1.71.0", {"center": v(51.34, 59.6) * mm, "majorRadius": 24.55 * mm, "minorRadius": 2 * mm, "majorAxis": v(-0.65, -0.76)});
            skEllipse(sketch, "E133.1.72.0", {"center": v(46.44, 63.39) * mm, "majorRadius": 24.55 * mm, "minorRadius": 2 * mm, "majorAxis": v(-0.59, -0.8)});
            skEllipse(sketch, "E133.1.73.0", {"center": v(41.27, 66.77) * mm, "majorRadius": 24.55 * mm, "minorRadius": 2 * mm, "majorAxis": v(-0.52, -0.85)});
            skEllipse(sketch, "E133.1.74.0", {"center": v(35.84, 69.74) * mm, "majorRadius": 24.55 * mm, "minorRadius": 2 * mm, "majorAxis": v(-0.45, -0.9)});
            skEllipse(sketch, "E134.1.75.0", {"center": v(30.2, 72.27) * mm, "majorRadius": 24.55 * mm, "minorRadius": 2 * mm, "majorAxis": v(-0.38, -0.92)});
            skEllipse(sketch, "E134.1.76.0", {"center": v(24.38, 74.35) * mm, "majorRadius": 24.55 * mm, "minorRadius": 2 * mm, "majorAxis": v(-0.3, -0.95)});
            skEllipse(sketch, "E134.1.77.0", {"center": v(18.4, 75.97) * mm, "majorRadius": 24.55 * mm, "minorRadius": 2 * mm, "majorAxis": v(-0.23, -0.97)});
            skEllipse(sketch, "E134.1.78.0", {"center": v(12.33, 77.12) * mm, "majorRadius": 24.55 * mm, "minorRadius": 2 * mm, "majorAxis": v(-0.16, -0.99)});
            skEllipse(sketch, "E134.1.79.0", {"center": v(6.18, 77.78) * mm, "majorRadius": 24.55 * mm, "minorRadius": 2 * mm, "majorAxis": v(-0.08, -1)});
            skSolve(sketch);
        }
        {
            var Q0;
            Q0=makeQuery(id+"F20.imprint","IMPRINT",FACE,{"disambiguationData":[TD([[makeQuery(id+"F20.imprint","IMPRINT",EDGE,{"derivedFrom":sQuery(id+"F20.wireOp",EDGE,"E125.0")}),-1.0]])]});
            extrude(context, id + "F21", {"entities" : qUnion([Q0]), "operationType" : NewBodyOperationType.REMOVE, "oppositeDirection" : true, "depth" : .1 * mm, "offsetDistance" : 25 * mm});
        }
    });
